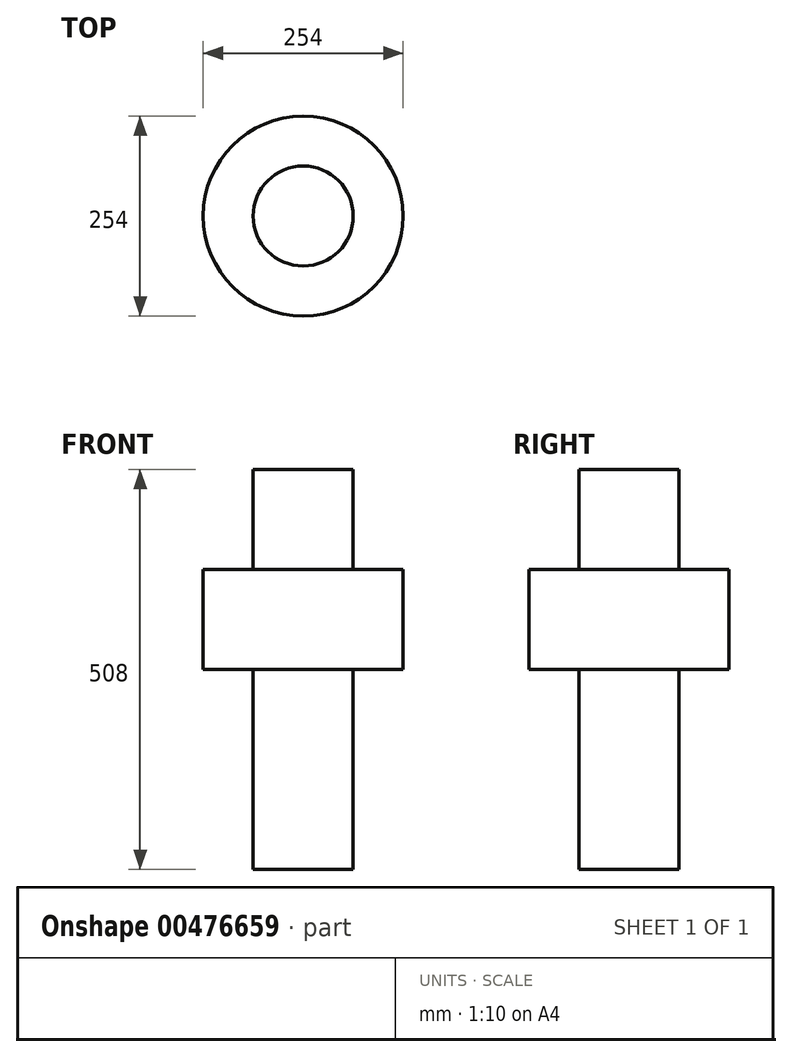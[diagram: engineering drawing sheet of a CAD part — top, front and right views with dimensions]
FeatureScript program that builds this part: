
annotation { "Feature Type Name" : "Feature", "Feature Type Description" : "" }
export const myFeature = defineFeature(function(context is Context, id is Id, definition is map)
    precondition{}
    {
        {
            var Q0;
            Q0=qCreatedBy(makeId("Top.planeOp"),FACE);
            var sketch = newSketch(context, id + "F0", { "sketchPlane" : qUnion([Q0])});
            skCircle(sketch, "E0", {"center": v(0, 0) * mm, "radius": 63.5 * mm});
            skSolve(sketch);
        }
        {
            var Q0;
            Q0=makeQuery(id+"F0.imprint","IMPRINT",FACE,{"disambiguationData":[TD([[makeQuery(id+"F0.imprint","IMPRINT",EDGE,{"derivedFrom":sQuery(id+"F0.wireOp",EDGE,"E0")}),1.0]])]});
            extrude(context, id + "F1", {"entities" : qUnion([Q0]), "depth" : 508 * mm});
        }
        {
            var Q0;
            Q0=makeQuery(id+"F1.opExtrude","CAP_FACE",FACE,{"disambiguationData":[OSD([sQuery(id+"F0.wireOp",EDGE,"E0")])],"isStart":false});
            cPlane(context, id + "F2", {"entities" : qUnion([Q0]), "cplaneType" : CPlaneType.OFFSET, "offset" : 127 * mm, "oppositeDirection" : true, "width" : 152.4 * mm, "height" : 152.4 * mm});
        }
        {
            var Q0;
            Q0=qCreatedBy(id+"F2.planeOp",FACE);
            var sketch = newSketch(context, id + "F3", { "sketchPlane" : qUnion([Q0])});
            skCircle(sketch, "E1.0", {"center": v(0, 0) * mm, "radius": 63.5 * mm, "construction": true});
            skCircle(sketch, "E2", {"center": v(0, 0) * mm, "radius": 127 * mm});
            skSolve(sketch);
        }
        {
            var Q0;
            Q0 = qSketchRegion(id + "F3", true);
            extrude(context, id + "F4", {"entities" : qUnion([Q0]), "operationType" : NewBodyOperationType.ADD, "oppositeDirection" : true, "depth" : 127 * mm});
        }
    });
